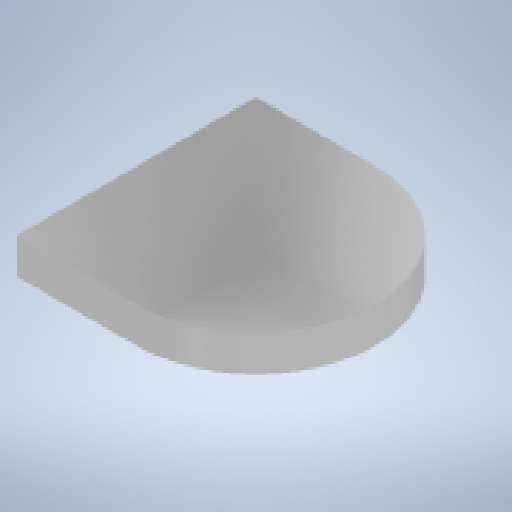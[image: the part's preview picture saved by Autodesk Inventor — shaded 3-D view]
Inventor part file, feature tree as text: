
AUTODESK INVENTOR PART (.ipt)
format: ipt  version: 2024 (Build 280153000, 153)  size: 142,336 bytes
history: native  units: mm
features: extrude x2, sketch x2, other x1
ambient origin geometry x8: Origin, YZ Plane, XZ Plane, XY Plane, X Axis, Y Axis, Z Axis, Center Point
bodies: Body1 (feature_tree)
feature tree (5):
  other  "ソリッド1"
  extrude  "押し出し1"  Depth=20.0mm
  extrude  "押し出し2"  Depth=3.0mm TaperAngle=0.0deg
  sketch  "スケッチ1"
  sketch  "スケッチ2"
